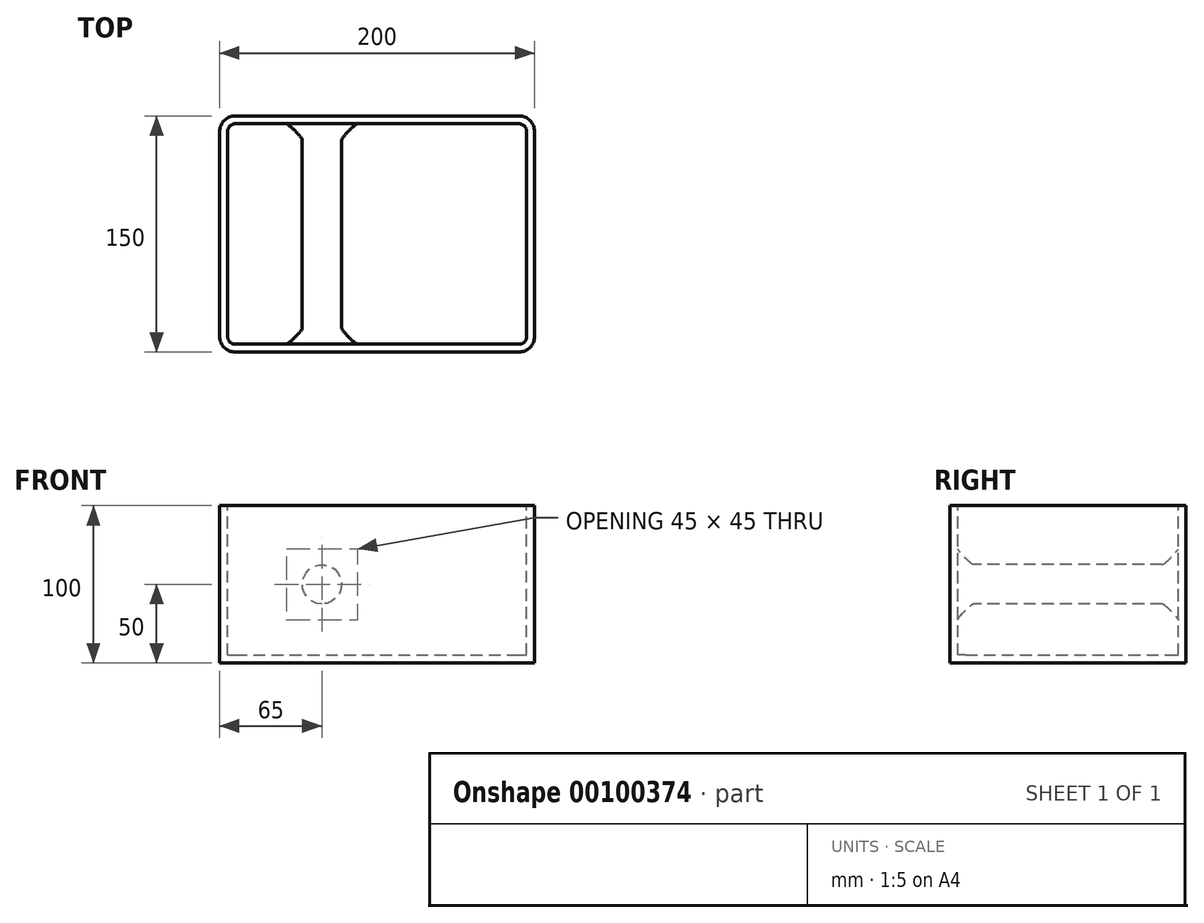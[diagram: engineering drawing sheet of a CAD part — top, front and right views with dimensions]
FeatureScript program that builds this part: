
annotation { "Feature Type Name" : "Feature", "Feature Type Description" : "" }
export const myFeature = defineFeature(function(context is Context, id is Id, definition is map)
    precondition{}
    {
        {
            var Q0;
            Q0=qCreatedBy(makeId("Front.planeOp"),FACE);
            var sketch = newSketch(context, id + "F0", { "sketchPlane" : qUnion([Q0])});
            skLineSegment(sketch, "E0.bottom", {"start": v(-100, -50) * mm, "end": v(100, -50) * mm});
            skLineSegment(sketch, "E0.top", {"start": v(-100, 50) * mm, "end": v(100, 50) * mm});
            skLineSegment(sketch, "E0.left", {"start": v(-100, -50) * mm, "end": v(-100, 50) * mm});
            skLineSegment(sketch, "E0.right", {"start": v(100, -50) * mm, "end": v(100, 50) * mm});
            skPoint(sketch, "E0.middle", {"position": v(0, 0) * mm});
            skSolve(sketch);
        }
        {
            var Q0;
            Q0 = qSketchRegion(id + "F0", true);
            extrude(context, id + "F1", {"entities" : qUnion([Q0]), "endBound" : BoundingType.SYMMETRIC, "depth" : 150 * mm});
        }
        {
            var Q0;
            Q0=makeQuery(id+"F1.opExtrude","CAP_EDGE",EDGE,{"disambiguationData":[OSD([sQuery(id+"F0.wireOp",EDGE,"E0.left")])],"isStart":false});
            var Q1;
            Q1=makeQuery(id+"F1.opExtrude","CAP_EDGE",EDGE,{"disambiguationData":[OSD([sQuery(id+"F0.wireOp",EDGE,"E0.right")])],"isStart":false});
            var Q2;
            Q2=makeQuery(id+"F1.opExtrude","CAP_EDGE",EDGE,{"disambiguationData":[OSD([sQuery(id+"F0.wireOp",EDGE,"E0.right")])],"isStart":true});
            var Q3;
            Q3=makeQuery(id+"F1.opExtrude","CAP_EDGE",EDGE,{"disambiguationData":[OSD([sQuery(id+"F0.wireOp",EDGE,"E0.left")])],"isStart":true});
            fillet(context, id + "F2", {"entities" : qUnion([Q0, Q1, Q2, Q3]), "radius" : 10 * mm, "tangentPropagation" : true, "allowEdgeOverflow" : false});
        }
        {
            var Q0;
            Q0=makeQuery(id+"F1.opExtrude","SWEPT_FACE",FACE,{"disambiguationData":[OSD([sQuery(id+"F0.wireOp",EDGE,"E0.top")])]});
            var Q1;
            Q1=makeQuery(id+"F1.opExtrude","SWEPT_BODY",BODY,{"disambiguationData":[OSD([sQuery(id+"F0.wireOp",EDGE,"E0.bottom"),sQuery(id+"F0.wireOp",EDGE,"E0.top"),sQuery(id+"F0.wireOp",EDGE,"E0.left"),sQuery(id+"F0.wireOp",EDGE,"E0.right")])]});
            shell(context, id + "F3", {"entities" : qUnion([Q0]), "parts" : qUnion([Q1]), "thickness" : 5 * mm});
        }
        {
            var Q0;
            Q0=makeQuery(id+"F1.opExtrude","CAP_FACE",FACE,{"disambiguationData":[OSD([sQuery(id+"F0.wireOp",EDGE,"E0.bottom"),sQuery(id+"F0.wireOp",EDGE,"E0.top"),sQuery(id+"F0.wireOp",EDGE,"E0.left"),sQuery(id+"F0.wireOp",EDGE,"E0.right")])],"isStart":false});
            var sketch = newSketch(context, id + "F4", { "sketchPlane" : qUnion([Q0])});
            skLineSegment(sketch, "E1", {"start": v(-90, 0) * mm, "end": v(-35, 0) * mm, "construction": true});
            skPoint(sketch, "E1.endSnap0", {"position": v(-90, 0) * mm});
            skLineSegment(sketch, "E2", {"start": v(-35, 0) * mm, "end": v(-35, -50) * mm, "construction": true});
            skCircle(sketch, "E3", {"center": v(-35, 0) * mm, "radius": 12.5 * mm});
            skSolve(sketch);
        }
        {
            var Q0;
            Q0 = qSketchRegion(id + "F4", true);
            var Q1;
            {var subQ0=sQuery(id+"F0.wireOp",EDGE,"E0.right");var subQ1=sQuery(id+"F0.wireOp",EDGE,"E0.left");var subQ2=sQuery(id+"F0.wireOp",EDGE,"E0.top");var subQ3=sQuery(id+"F0.wireOp",EDGE,"E0.bottom");Q1=makeQuery(id+"F3.opShell","OFFSET_FACE",FACE,{"disambiguationData":[OSD([subQ3,subQ2,subQ1,subQ0]),TDD([makeQuery(id+"F1.opExtrude","CAP_FACE",FACE,{"disambiguationData":[OSD([subQ3,subQ2,subQ1,subQ0])],"isStart":true})])]});}
            extrude(context, id + "F5", {"entities" : qUnion([Q0]), "operationType" : NewBodyOperationType.ADD, "endBound" : BoundingType.UP_TO_SURFACE, "oppositeDirection" : true, "endBoundEntityFace" : qUnion([Q1]), "depth" : 25 * mm});
        }
        {
            var Q0;
            Q0=makeQuery(id+"F5.opExtrude","SWEPT_FACE",FACE,{"disambiguationData":[OSD([sQuery(id+"F4.wireOp",EDGE,"E3")])]});
            fillet(context, id + "F6", {"entities" : qUnion([Q0]), "radius" : 10 * mm, "tangentPropagation" : true, "rho" : 0.1, "crossSection" : FilletCrossSection.CONIC, "allowEdgeOverflow" : false});
        }
    });
